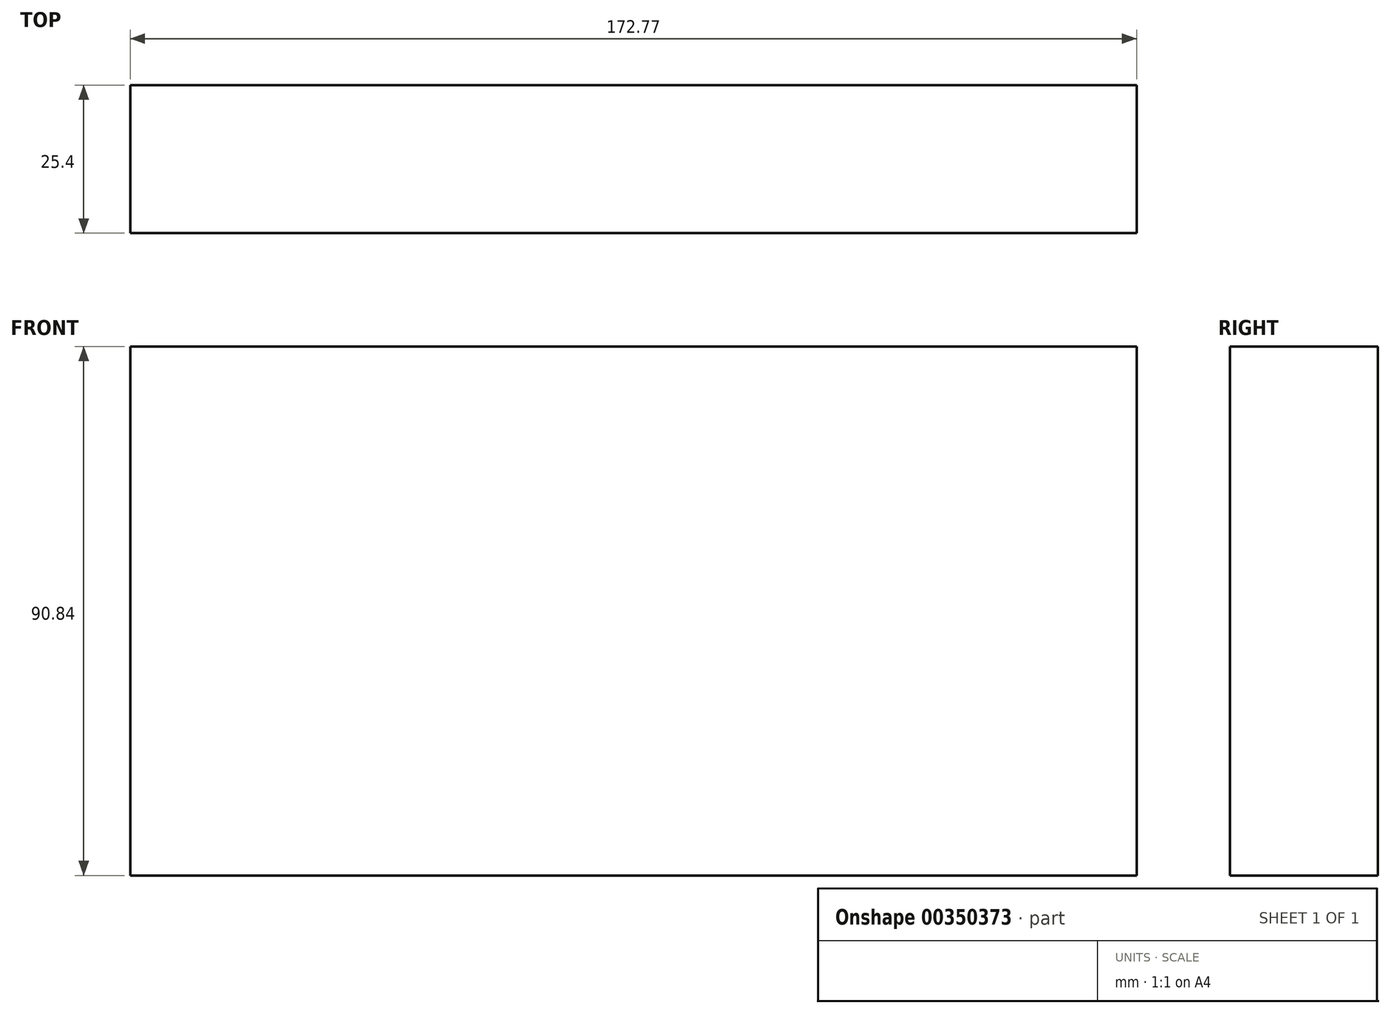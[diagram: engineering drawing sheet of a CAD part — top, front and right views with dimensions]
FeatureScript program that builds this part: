
annotation { "Feature Type Name" : "Feature", "Feature Type Description" : "" }
export const myFeature = defineFeature(function(context is Context, id is Id, definition is map)
    precondition{}
    {
        {
            var Q0;
            Q0=qCreatedBy(makeId("Front.planeOp"),FACE);
            var sketch = newSketch(context, id + "F0", { "sketchPlane" : qUnion([Q0])});
            skLineSegment(sketch, "E0", {"start": v(-100.84, 41.54) * mm, "end": v(71.93, 41.54) * mm});
            skLineSegment(sketch, "E1", {"start": v(71.93, 41.54) * mm, "end": v(71.93, -49.3) * mm});
            skLineSegment(sketch, "E2", {"start": v(71.93, -49.3) * mm, "end": v(-100.84, -49.3) * mm});
            skLineSegment(sketch, "E3", {"start": v(-100.84, -49.3) * mm, "end": v(-100.84, 41.54) * mm});
            skSolve(sketch);
        }
        {
            var Q0;
            Q0=makeQuery(id+"F0.imprint","IMPRINT",FACE,{"disambiguationData":[TD([[makeQuery(id+"F0.imprint","IMPRINT",EDGE,{"derivedFrom":sQuery(id+"F0.wireOp",EDGE,"E0")}),-1.0]])]});
            extrude(context, id + "F1", {"entities" : qUnion([Q0]), "depth" : 25.4 * mm});
        }
    });
